# Revit family: Electronics_Impera_Biamp_Connect-X-MP6
name_source: partatom
category: Communication Devices
units: mm (PartAtom-declared; Revit-internal decimal feet)

## family parameters
Cut with Voids When Loaded = No
Host = Face
Maintain Annotation Orientation = No
OmniClass Number = 23.85.10.11
OmniClass Title = Audio Information, Sound Signals
Part Type = Normal
Room Calculation Point = No
Round Connector Dimension = Use Diameter
Shared = No

## types (1)
- Connect-X MP6
    Autosense = Yes
    Baud Rate = 1200 – 115200 bit/sec
    Connector Description = RJ-45 Input, Each I/O can draw up to 24DC/500mA
    Data Bits = 7,8
    Default Elevation = 1219 mm
    Depth = 92 mm
    Description = Impera Connect-X MP6 Multiport Extender
    Height = 22 mm  [stored 0.0721785 ft]
    Housing Material = Biamp - Plastic - Black
    I/O Quantity = 3
    IR Frequency Range = 381 Hz to 500 kHz
    Included Accessories = Mounting screws and zipties
    Manufacturer = Biamp
    Max Current = 0.5 A
    Max Voltage = 24 VDC
    Model = Connect-X MP6
    Number of Ports = 1 (bidirectional),2 (unidirectional)
    Number of third-party devices supported = 2
    Output Type = Open drain
    Parity = Even, Odd, None
    Port Speed = 10/100 Mbps
    Power = PoE (IEEE 802.3at Class 1, 4W)
    Product Documentation Link = https://downloads.biamp.com
    Product Page URL = https://www.biamp.com
    Product data url = https://bimobject.com
    Sense High = > 4 VDC
    Sense Low = < 1 VDC
    Stop Bits = 1, 1.5, 2
    URL = https://www.biamp.com
    Version = 1
    Weight = 0.24 lb
    Width = 127 mm

note: [stored X ft] marks values corroborated as IEEE doubles in the binary element streams (Revit-internal decimal feet)

## geometry (parser evidence)
native form markers: Sweep x1
no freeform markers — native parametric forms only
